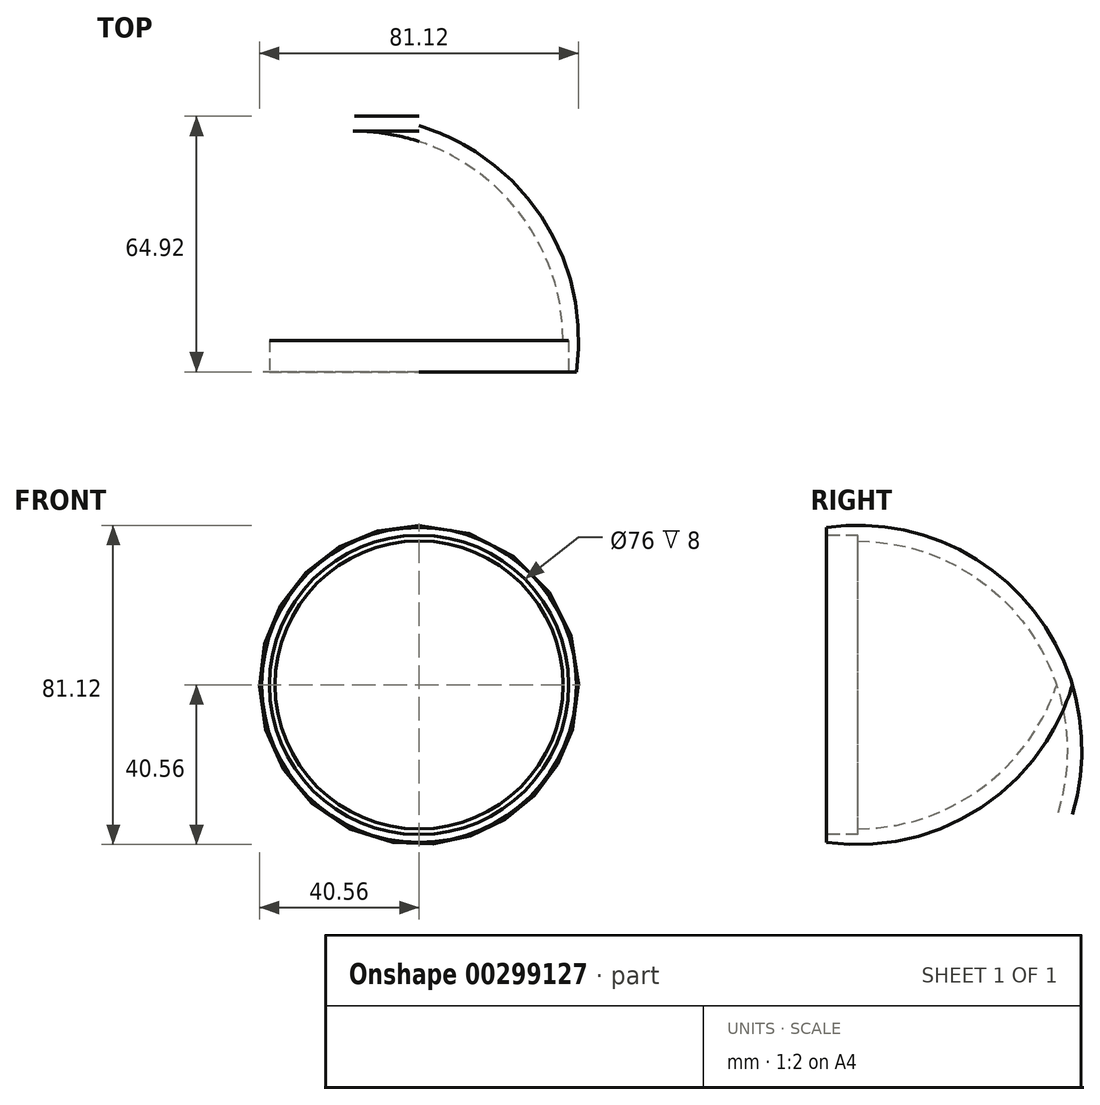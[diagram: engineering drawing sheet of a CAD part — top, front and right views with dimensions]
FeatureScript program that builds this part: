
annotation { "Feature Type Name" : "Feature", "Feature Type Description" : "" }
export const myFeature = defineFeature(function(context is Context, id is Id, definition is map)
    precondition{}
    {
        {
            var Q0;
            Q0=qCreatedBy(makeId("Top.planeOp"),FACE);
            var sketch = newSketch(context, id + "F0", { "sketchPlane" : qUnion([Q0])});
            skLineSegment(sketch, "E0", {"start": v(0, 0) * mm, "end": v(36, 0) * mm});
            skLineSegment(sketch, "E1", {"start": v(36, 0) * mm, "end": v(40, 0) * mm});
            skLineSegment(sketch, "E2", {"start": v(0, 0) * mm, "end": v(-36, 0) * mm});
            skLineSegment(sketch, "E3", {"start": v(-36, 0) * mm, "end": v(-40, 0) * mm});
            skLineSegment(sketch, "E4", {"start": v(0, 0) * mm, "end": v(0, 58.5) * mm});
            skLineSegment(sketch, "E5", {"start": v(0, 58.5) * mm, "end": v(0, 62.5) * mm});
            skLineSegment(sketch, "E6", {"start": v(-36, 0) * mm, "end": v(-23.38, 0) * mm});
            skLineSegment(sketch, "E7", {"start": v(-23.38, 0) * mm, "end": v(-20.89, 0) * mm});
            skLineSegment(sketch, "E8", {"start": v(36, 0) * mm, "end": v(23.38, 0) * mm});
            skLineSegment(sketch, "E9", {"start": v(23.38, 0) * mm, "end": v(20.89, 0) * mm});
            skArc(sketch, "E10", {"start": v(0, 62.5) * mm, "mid": v(-31.57, 38.65) * mm, "end": v(-40, 0) * mm});
            skArc(sketch, "E11", {"start": v(40, 0) * mm, "mid": v(31.57, 38.65) * mm, "end": v(0, 62.5) * mm});
            skArc(sketch, "E12", {"start": v(36, 0) * mm, "mid": v(28.68, 35.82) * mm, "end": v(0, 58.5) * mm});
            skArc(sketch, "E13", {"start": v(0, 58.5) * mm, "mid": v(-28.68, 35.82) * mm, "end": v(-36, 0) * mm});
            skSolve(sketch);
        }
        {
            var Q0;
            Q0=makeQuery(id+"F0.imprint","IMPRINT",FACE,{"disambiguationData":[TD([[makeQuery(id+"F0.imprint","IMPRINT",EDGE,{"derivedFrom":sQuery(id+"F0.wireOp",EDGE,"E3")}),-1.0]])]});
            var Q1;
            Q1=sQuery(id+"F0.wireOp",EDGE,"E4");
            revolve(context, id + "F1", {"entities" : qUnion([Q0]), "axis" : qUnion([Q1]), "revolveType" : RevolveType.FULL});
        }
        {
            var Q0;
            Q0=makeQuery(id+"F1.opRevolve","SWEPT_FACE",FACE,{"disambiguationData":[OSD([sQuery(id+"F0.wireOp",EDGE,"E3")])]});
            var sketch = newSketch(context, id + "F2", { "sketchPlane" : qUnion([Q0])});
            skCircle(sketch, "E14", {"center": v(0, 0) * mm, "radius": 36 * mm});
            skCircle(sketch, "E15", {"center": v(0, 0) * mm, "radius": 38 * mm});
            skSolve(sketch);
        }
        {
            var Q0;
            Q0=makeQuery(id+"F2.imprint","IMPRINT",FACE,{"disambiguationData":[TD([[makeQuery(id+"F2.imprint","IMPRINT",EDGE,{"derivedFrom":sQuery(id+"F2.wireOp",EDGE,"E14")}),-1.0]])]});
            extrude(context, id + "F3", {"entities" : qUnion([Q0]), "operationType" : NewBodyOperationType.REMOVE, "oppositeDirection" : true, "depth" : 8 * mm});
        }
    });
